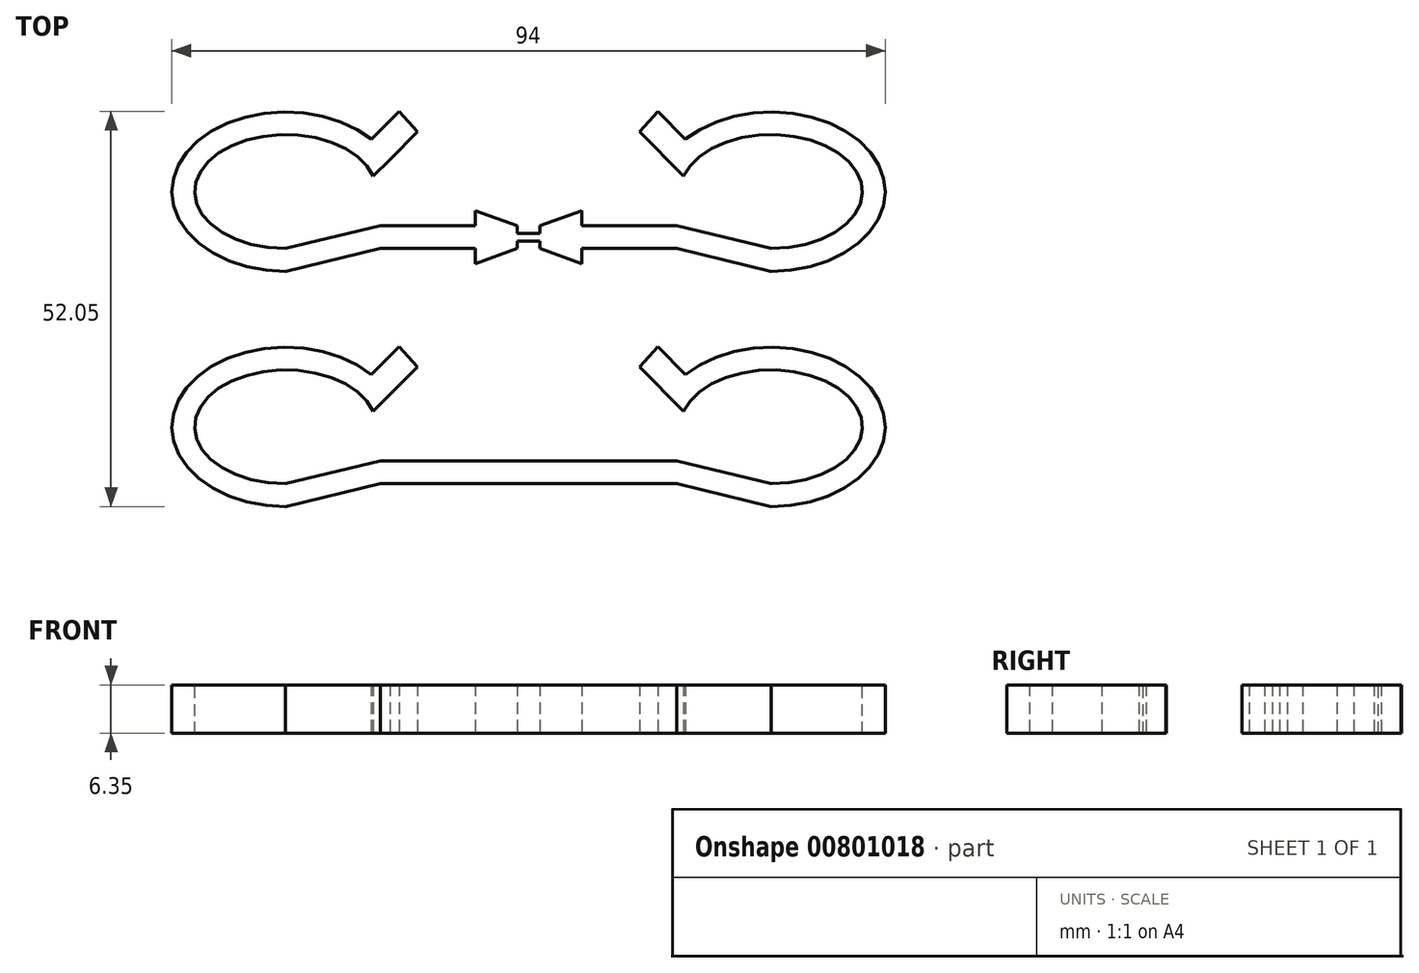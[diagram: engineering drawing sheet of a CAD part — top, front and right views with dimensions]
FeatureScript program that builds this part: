
annotation { "Feature Type Name" : "Feature", "Feature Type Description" : "" }
export const myFeature = defineFeature(function(context is Context, id is Id, definition is map)
    precondition{}
    {
        {
            var Q0;
            Q0=qCreatedBy(makeId("Top.planeOp"),FACE);
            var sketch = newSketch(context, id + "F0", { "sketchPlane" : qUnion([Q0])});
            skLineSegment(sketch, "E0", {"start": v(-20.45, -13.5) * mm, "end": v(-14.62, -7.66) * mm});
            skEllipticalArc(sketch, "E1", {});
            skEllipticalArc(sketch, "E2", {});
            skLineSegment(sketch, "E3", {"start": v(-14.62, -7.66) * mm, "end": v(-17.06, -4.97) * mm});
            skLineSegment(sketch, "E4", {"start": v(0, -23.03) * mm, "end": v(-19.5, -23.03) * mm});
            skLineSegment(sketch, "E5", {"start": v(-32, -26.03) * mm, "end": v(-19.5, -23.03) * mm});
            skLineSegment(sketch, "E6", {"start": v(-32, -23.03) * mm, "end": v(-19.5, -20.03) * mm});
            skLineSegment(sketch, "E7", {"start": v(-19.5, -20.03) * mm, "end": v(0, -20.03) * mm});
            skLineSegment(sketch, "E8", {"start": v(-20.7, -8.63) * mm, "end": v(-17.05, -4.98) * mm});
            skEllipticalArc(sketch, "E9", {});
            skEllipticalArc(sketch, "E10", {});
            skLineSegment(sketch, "E11", {"start": v(0, -23.03) * mm, "end": v(19.5, -23.03) * mm});
            skLineSegment(sketch, "E12", {"start": v(32, -26.03) * mm, "end": v(19.5, -23.03) * mm});
            skLineSegment(sketch, "E13", {"start": v(32, -23.03) * mm, "end": v(19.5, -20.03) * mm});
            skLineSegment(sketch, "E14", {"start": v(19.5, -20.03) * mm, "end": v(0, -20.03) * mm});
            skLineSegment(sketch, "E15", {"start": v(-20.45, 17.51) * mm, "end": v(-14.62, 23.34) * mm});
            skEllipticalArc(sketch, "E16", {});
            skEllipticalArc(sketch, "E17", {});
            skLineSegment(sketch, "E18", {"start": v(-14.62, 23.34) * mm, "end": v(-17.06, 26.03) * mm});
            skLineSegment(sketch, "E19", {"start": v(-32, 4.97) * mm, "end": v(-19.5, 7.97) * mm});
            skLineSegment(sketch, "E20", {"start": v(-32, 7.97) * mm, "end": v(-19.5, 10.97) * mm});
            skLineSegment(sketch, "E21", {"start": v(-20.7, 22.37) * mm, "end": v(-17.05, 26.02) * mm});
            skLineSegment(sketch, "E22", {"start": v(-1.5, 10.97) * mm, "end": v(-7, 12.97) * mm});
            skLineSegment(sketch, "E23", {"start": v(-7, 12.97) * mm, "end": v(-7, 10.97) * mm});
            skLineSegment(sketch, "E24", {"start": v(-1.5, 7.97) * mm, "end": v(-7, 5.97) * mm});
            skLineSegment(sketch, "E25", {"start": v(-7, 5.97) * mm, "end": v(-7, 7.97) * mm});
            skLineSegment(sketch, "E26", {"start": v(-1.5, 10.97) * mm, "end": v(-1.5, 9.97) * mm});
            skLineSegment(sketch, "E27", {"start": v(-1.5, 9.97) * mm, "end": v(0, 9.97) * mm});
            skLineSegment(sketch, "E28", {"start": v(-1.5, 7.97) * mm, "end": v(-1.5, 8.97) * mm});
            skLineSegment(sketch, "E29", {"start": v(-1.5, 8.97) * mm, "end": v(0, 8.97) * mm});
            skLineSegment(sketch, "E30", {"start": v(17.05, 26.02) * mm, "end": v(17.06, 26.03) * mm});
            skLineSegment(sketch, "E31", {"start": v(-19.5, 10.97) * mm, "end": v(-7, 10.97) * mm});
            skLineSegment(sketch, "E32", {"start": v(-19.5, 7.97) * mm, "end": v(-7, 7.97) * mm});
            skPoint(sketch, "E33", {"position": v(-44, -15.53) * mm});
            skPoint(sketch, "E34", {"position": v(-32, -8.03) * mm});
            skPoint(sketch, "E35", {"position": v(-32, -5.03) * mm});
            skPoint(sketch, "E36", {"position": v(-47, -15.53) * mm});
            skPoint(sketch, "E37", {"position": v(32, -8.03) * mm});
            skPoint(sketch, "E38", {"position": v(44, -15.53) * mm});
            skPoint(sketch, "E39", {"position": v(32, -5.03) * mm});
            skPoint(sketch, "E40", {"position": v(47, -15.53) * mm});
            skEllipticalArc(sketch, "E41.trimOffspring", {});
            skLineSegment(sketch, "E42", {"start": v(19.5, -20.03) * mm, "end": v(32, -23.03) * mm});
            skEllipticalArc(sketch, "E43", {});
            skEllipticalArc(sketch, "E44", {});
            skEllipticalArc(sketch, "E45", {});
            skEllipticalArc(sketch, "E46.trimOffspring", {});
            skLineSegment(sketch, "E47", {"start": v(32, -8.03) * mm, "end": v(30, -8.14) * mm});
            skEllipticalArc(sketch, "E48.trimOffspring", {});
            skLineSegment(sketch, "E49.MirrorCS", {"start": v(20.45, -13.5) * mm, "end": v(14.62, -7.66) * mm});
            skLineSegment(sketch, "E50.MirrorCS", {"start": v(14.62, -7.66) * mm, "end": v(17.06, -4.97) * mm});
            skLineSegment(sketch, "E51.MirrorCS", {"start": v(20.7, -8.63) * mm, "end": v(17.05, -4.98) * mm});
            skEllipticalArc(sketch, "E52.trimOffspring", {});
            skPoint(sketch, "E53", {"position": v(32, 22.97) * mm});
            skPoint(sketch, "E54", {"position": v(44, 15.47) * mm});
            skPoint(sketch, "E55", {"position": v(47, 15.47) * mm});
            skPoint(sketch, "E56", {"position": v(32, 25.97) * mm});
            skPoint(sketch, "E57.MirrorCS.end.orphan", {"position": v(17.05, 26.02) * mm});
            skPoint(sketch, "E57.MirrorCS.start.orphan", {"position": v(20.7, 22.37) * mm});
            skPoint(sketch, "E58.orphan", {"position": v(14.62, 23.34) * mm});
            skPoint(sketch, "E59.MirrorCS.start.orphan", {"position": v(20.45, 17.51) * mm});
            skPoint(sketch, "E60.orphan", {"position": v(20.45, 17.5) * mm});
            skPoint(sketch, "E61.trimOffspring.start.orphan", {"position": v(20.7, 22.38) * mm});
            skPoint(sketch, "E62.MirrorCS.start.orphan", {"position": v(32, 7.97) * mm});
            skPoint(sketch, "E63.MirrorCS.start.orphan", {"position": v(32, 4.97) * mm});
            skLineSegment(sketch, "E64.MirrorCS", {"start": v(1.5, 10.97) * mm, "end": v(7, 12.97) * mm});
            skLineSegment(sketch, "E65.MirrorCS", {"start": v(1.5, 9.97) * mm, "end": v(0, 9.97) * mm});
            skLineSegment(sketch, "E66.MirrorCS", {"start": v(1.5, 10.97) * mm, "end": v(1.5, 9.97) * mm});
            skLineSegment(sketch, "E67.MirrorCS", {"start": v(1.5, 8.97) * mm, "end": v(0, 8.97) * mm});
            skLineSegment(sketch, "E68.MirrorCS", {"start": v(1.5, 7.97) * mm, "end": v(7, 5.97) * mm});
            skLineSegment(sketch, "E69.MirrorCS", {"start": v(19.5, 7.97) * mm, "end": v(7, 7.97) * mm});
            skLineSegment(sketch, "E70.MirrorCS", {"start": v(1.5, 7.97) * mm, "end": v(1.5, 8.97) * mm});
            skLineSegment(sketch, "E71.MirrorCS", {"start": v(7, 5.97) * mm, "end": v(7, 7.97) * mm});
            skLineSegment(sketch, "E72.MirrorCS", {"start": v(7, 12.97) * mm, "end": v(7, 10.97) * mm});
            skLineSegment(sketch, "E73.MirrorCS", {"start": v(19.5, 10.97) * mm, "end": v(7, 10.97) * mm});
            skPoint(sketch, "E74", {"position": v(-32, 22.97) * mm});
            skPoint(sketch, "E75", {"position": v(-44, 15.47) * mm});
            skPoint(sketch, "E76", {"position": v(-47, 15.47) * mm});
            skPoint(sketch, "E77", {"position": v(-32, 25.97) * mm});
            skEllipticalArc(sketch, "E78.trimOffspring", {});
            skLineSegment(sketch, "E79", {"start": v(-20.45, 17.5) * mm, "end": v(-14.62, 23.34) * mm});
            skLineSegment(sketch, "E80.MirrorCS", {"start": v(20.7, 22.37) * mm, "end": v(17.05, 26.02) * mm});
            skLineSegment(sketch, "E81.MirrorCS", {"start": v(14.62, 23.34) * mm, "end": v(17.06, 26.03) * mm});
            skEllipticalArc(sketch, "E82.MirrorCS", {});
            skEllipticalArc(sketch, "E83.MirrorCS", {});
            skLineSegment(sketch, "E84.MirrorCS", {"start": v(32, 7.97) * mm, "end": v(19.5, 10.97) * mm});
            skLineSegment(sketch, "E85.MirrorCS", {"start": v(32, 4.97) * mm, "end": v(19.5, 7.97) * mm});
            skPoint(sketch, "E86.MirrorCS.end.orphan", {"position": v(-19.5, 7.97) * mm});
            skPoint(sketch, "E86.MirrorCS.start.orphan", {"position": v(-19.5, 10.97) * mm});
            skLineSegment(sketch, "E87", {"start": v(20.7, 22.38) * mm, "end": v(17.06, 26.03) * mm});
            skEllipticalArc(sketch, "E88.trimOffspring", {});
            skLineSegment(sketch, "E89", {"start": v(7, 10.97) * mm, "end": v(19.5, 10.97) * mm});
            skLineSegment(sketch, "E90", {"start": v(20.45, 17.5) * mm, "end": v(14.62, 23.34) * mm});
            const initialGuessF0  = {"E1": [-0.032, -0.01553033, -1, 0, 0.012, 0.0075, 3.416708, 1.5707963267948966], "E2": [-0.032, -0.01553033, -14.999986, 0, 0.014999986, 0.0105, 3.859575, 7.853982], "E9": [0.032, -0.01553033, 1, 0, 0.012, 0.0075, 4.71238898038469, 2.8664773071795864], "E10": [0.032, -0.01553033, 14.999986, 0, 0.014999986, 0.0105, -1.570796692820414, 2.4236103071795863], "E16": [-0.032, 0.015469670000000001, -12, 0, 0.012, 0.0075, 3.416708, 7.853982], "E17": [-0.032, 0.015469670000000001, -14.999986, 0, 0.014999986, 0.0105, 3.859575, 7.853982], "E1": [-0.032, -0.01553033, -1, 0, 0.012, 0.0075, 3.416708, 1.5707963267948966], "E2": [-0.032, -0.01553033, -1, 0, 0.014999986, 0.0105, 3.8586865618368624, 1.5707963267948966], "E9": [0.032, -0.01553033, 1, 0, 0.012, 0.0075, 4.71238898038469, 2.8664773071795864], "E41.trimOffspring": [0.032, -0.015530329999997075, 1, 0, 0.014999986, 0.0105, 4.71238898038469, 2.424498745343496], "E43": [0.032, -0.01553033, 1, 0, 0.012, 0.0075, 4.71238898038469, 1.5707963267948966], "E41.trimOffspring": [0.032, -0.015530329999997075, 1, 0, 0.014999986, 0.0105, 4.71238898038469, 2.424498745343496], "E44": [0.032, -0.01553033, 0, 1, 0.0105, 0.014999986, 3.141592653589793, 0.8537024185482291], "E45": [0.032, -0.01553033, 0, 1, 0.0075, 0.012, 3.141592653589793, 6.283185307179586], "E46.trimOffspring": [0.032, -0.015530329999997074, 1, 0, 0.014999986, 0.0105, 4.71238898038469, 1.5707963267948966], "E48.trimOffspring": [0.032, -0.015530329999997074, 1, 0, 0.014999986, 0.0105, 2.423610307179587, 2.424498745343127], "E10": [0.032, -0.01553033, 1, 0, 0.014999986, 0.0105, 4.71238898038469, 2.424498745342724], "E52.trimOffspring": [0.032, -0.01553033, 0, 1, 0.0075, 0.012, 0.16741226436513656, 1.2956809803846898], "E16": [-0.032, 0.015469670000000001, -1, 0, 0.012, 0.0075, 3.416708, 1.5707963267948966], "E17": [-0.032, 0.015469670000000001, -1, 0, 0.014999986, 0.0105, 3.8586865618368624, 1.5707963267948966], "E78.trimOffspring": [-0.032, 0.015469670000000001, -1, 0, 0.014999986, 0.0105, 3.555565494325255, 3.5557762907210475], "E82.MirrorCS": [0.032, 0.015469670000000001, 1, 0, 0.012, 0.0075, 4.71238898038469, 2.866477307179588], "E83.MirrorCS": [0.032, 0.015469670000000001, 1, 0, 0.014999986, 0.0105, 4.71238898038469, 2.424498745342724], "E82.MirrorCS": [0.032, 0.015469670000000001, 1, 0, 0.012, 0.0075, 4.71238898038469, 2.866477307179588], "E88.trimOffspring": [0.032, 0.015469670000000001, 1, 0, 0.014999986, 0.0105, 4.71238898038469, 2.424498745342724], "E82.MirrorCS": [0.032, 0.015469670000000001, 1, 0, 0.012, 0.0075, 4.71238898038469, 2.866477307179588], "E83.MirrorCS": [0.032, 0.015469670000000001, 1, 0, 0.014999986, 0.0105, 4.71238898038469, 2.424498745342724]};
            skSetInitialGuess(sketch, initialGuessF0);
            skSolve(sketch);
        }
        {
            var Q0;
            {var subQ3=sQuery(id+"F0.wireOp",EDGE,"E0");Q0=makeQuery(id+"F0.imprint","IMPRINT",FACE,{"disambiguationData":[TD([[makeQuery(id+"F0.imprint","IMPRINT",EDGE,{"derivedFrom":subQ3}),1.0]])]});}
            extrude(context, id + "F1", {"entities" : qUnion([Q0]), "depth" : 6.35 * mm, "offsetDistance" : 25.4 * mm});
        }
        {
            var Q0;
            {var subQ0=sQuery(id+"F0.wireOp",EDGE,"E19");Q0=makeQuery(id+"F0.imprint","IMPRINT",FACE,{"disambiguationData":[TD([[makeQuery(id+"F0.imprint","IMPRINT",EDGE,{"derivedFrom":subQ0}),1.0]])]});}
            extrude(context, id + "F2", {"entities" : qUnion([Q0]), "depth" : 6.35 * mm, "offsetDistance" : 25.4 * mm});
        }
    });
